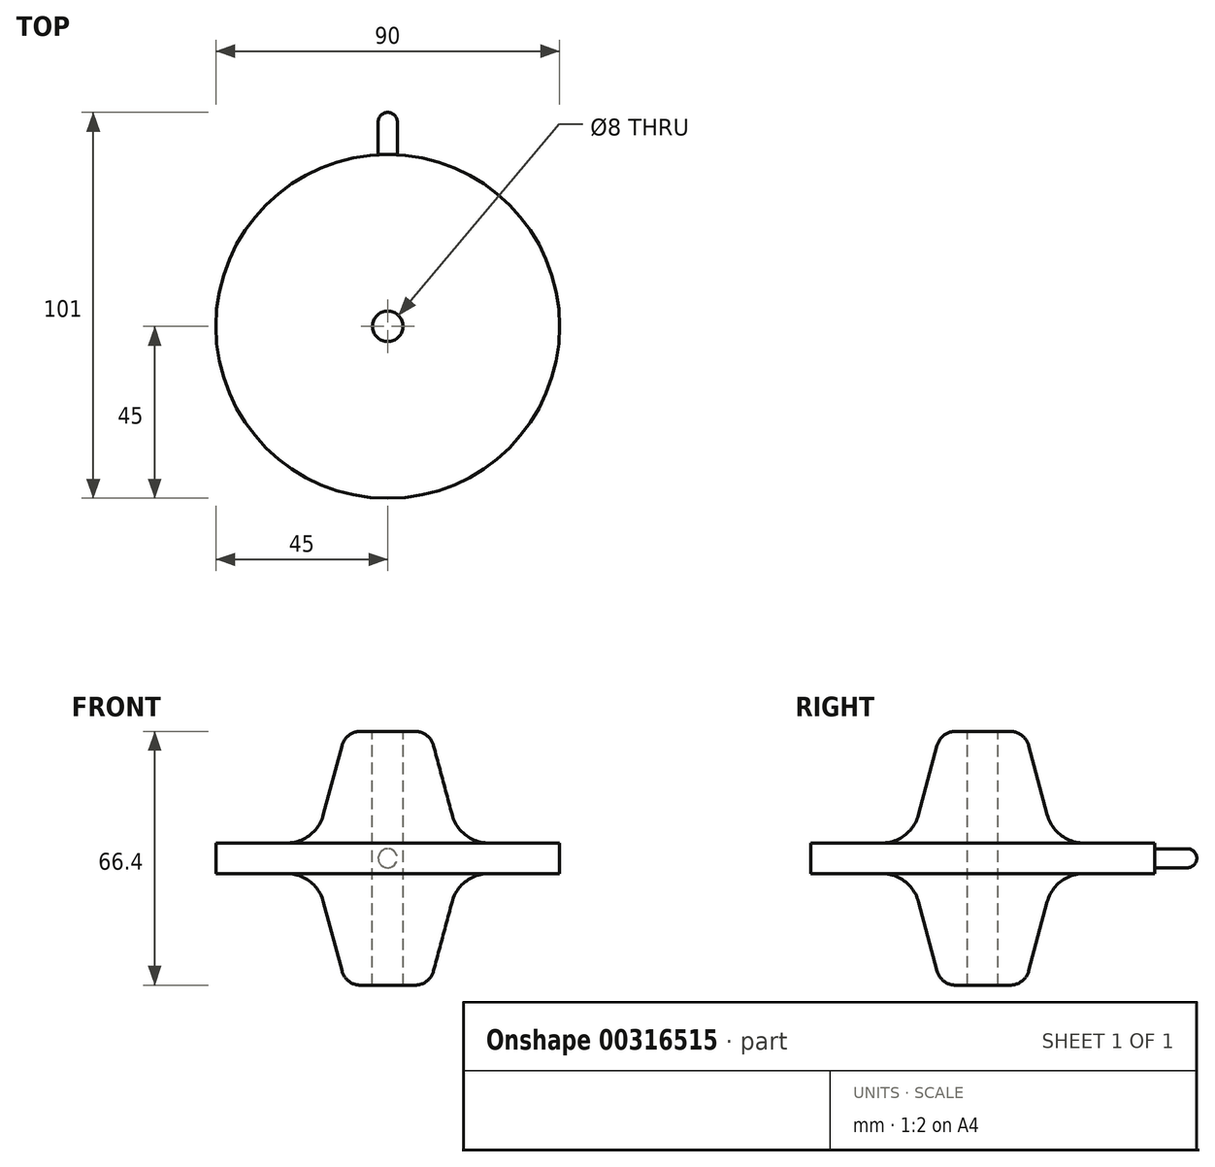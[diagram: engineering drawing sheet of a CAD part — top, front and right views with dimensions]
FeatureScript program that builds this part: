
annotation { "Feature Type Name" : "Feature", "Feature Type Description" : "" }
export const myFeature = defineFeature(function(context is Context, id is Id, definition is map)
    precondition{}
    {
        {
            var Q0;
            Q0=qCreatedBy(makeId("Right.planeOp"),FACE);
            var sketch = newSketch(context, id + "F0", { "sketchPlane" : qUnion([Q0])});
            skLineSegment(sketch, "E0", {"start": v(-44.32, 0) * mm, "end": v(43.47, 0) * mm, "construction": true});
            skLineSegment(sketch, "E1", {"start": v(0, 43.68) * mm, "end": v(0, -43.47) * mm, "construction": true});
            skLineSegment(sketch, "E2", {"start": v(-45, 0) * mm, "end": v(-45, 4) * mm});
            skLineSegment(sketch, "E3", {"start": v(-45, 4) * mm, "end": v(-26.5, 4) * mm});
            skLineSegment(sketch, "E4", {"start": v(-12, 29.5) * mm, "end": v(-16.84, 11.41) * mm});
            skPoint(sketch, "E5.visualSharp", {"position": v(-18.82, 4) * mm});
            skArc(sketch, "E5.filletArc", {"start": v(-26.5, 4) * mm, "mid": v(-20.4, 6.07) * mm, "end": v(-16.84, 11.41) * mm});
            skPoint(sketch, "E6.visualSharp", {"position": v(-11, 33.2) * mm});
            skArc(sketch, "E6.filletArc", {"start": v(-7.16, 33.2) * mm, "mid": v(-10.2, 32.17) * mm, "end": v(-12, 29.5) * mm});
            skLineSegment(sketch, "E7", {"start": v(-7.16, 33.2) * mm, "end": v(-4, 33.2) * mm});
            skLineSegment(sketch, "E8.MirrorCS", {"start": v(-7.16, -33.2) * mm, "end": v(-4, -33.2) * mm});
            skArc(sketch, "E9.MirrorCS", {"start": v(-7.16, -33.2) * mm, "mid": v(-10.2, -32.17) * mm, "end": v(-12, -29.5) * mm});
            skLineSegment(sketch, "E10.MirrorCS", {"start": v(-12, -29.5) * mm, "end": v(-16.84, -11.41) * mm});
            skArc(sketch, "E11.MirrorCS", {"start": v(-26.5, -4) * mm, "mid": v(-20.4, -6.07) * mm, "end": v(-16.84, -11.41) * mm});
            skLineSegment(sketch, "E12.MirrorCS", {"start": v(-45, -4) * mm, "end": v(-26.5, -4) * mm});
            skLineSegment(sketch, "E13.MirrorCS", {"start": v(-45, 0) * mm, "end": v(-45, -4) * mm});
            skLineSegment(sketch, "E14", {"start": v(-4, 33.2) * mm, "end": v(-4, -33.2) * mm});
            skSolve(sketch);
        }
        {
            var Q0;
            Q0=makeQuery(id+"F0.imprint","IMPRINT",FACE,{"disambiguationData":[TD([[makeQuery(id+"F0.imprint","IMPRINT",EDGE,{"derivedFrom":sQuery(id+"F0.wireOp",EDGE,"E2")}),-1.0]])]});
            var Q1;
            Q1=sQuery(id+"F0.wireOp",EDGE,"E1");
            revolve(context, id + "F1", {"entities" : qUnion([Q0]), "axis" : qUnion([Q1]), "revolveType" : RevolveType.FULL});
        }
        {
            var Q0;
            Q0=qCreatedBy(makeId("Right.planeOp"),FACE);
            var sketch = newSketch(context, id + "F2", { "sketchPlane" : qUnion([Q0])});
            skLineSegment(sketch, "E15.bottom", {"start": v(40.3, 2.5) * mm, "end": v(56, 2.5) * mm});
            skLineSegment(sketch, "E15.top", {"start": v(40.3, 0) * mm, "end": v(56, 0) * mm});
            skLineSegment(sketch, "E15.left", {"start": v(40.3, 2.5) * mm, "end": v(40.3, 0) * mm});
            skLineSegment(sketch, "E15.right", {"start": v(56, 2.5) * mm, "end": v(56, 0) * mm});
            skSolve(sketch);
        }
        {
            var Q0;
            Q0=makeQuery(id+"F2.imprint","IMPRINT",FACE,{"disambiguationData":[TD([[makeQuery(id+"F2.imprint","IMPRINT",EDGE,{"derivedFrom":sQuery(id+"F2.wireOp",EDGE,"E15.bottom")}),-1.0]])]});
            var Q1;
            Q1=sQuery(id+"F2.wireOp",EDGE,"E15.top");
            revolve(context, id + "F3", {"operationType" : NewBodyOperationType.ADD, "entities" : qUnion([Q0]), "axis" : qUnion([Q1]), "revolveType" : RevolveType.FULL});
        }
        {
            var Q0;
            Q0=makeQuery(id+"F3.opRevolve","SWEPT_EDGE",EDGE,{"disambiguationData":[OSD([sQuery(id+"F2.wireOp",EDGE,"E15.bottom"),sQuery(id+"F2.wireOp",EDGE,"E15.right")])]});
            fillet(context, id + "F4", {"entities" : qUnion([Q0]), "radius" : 2.5 * mm, "tangentPropagation" : true, "allowEdgeOverflow" : false});
        }
    });
